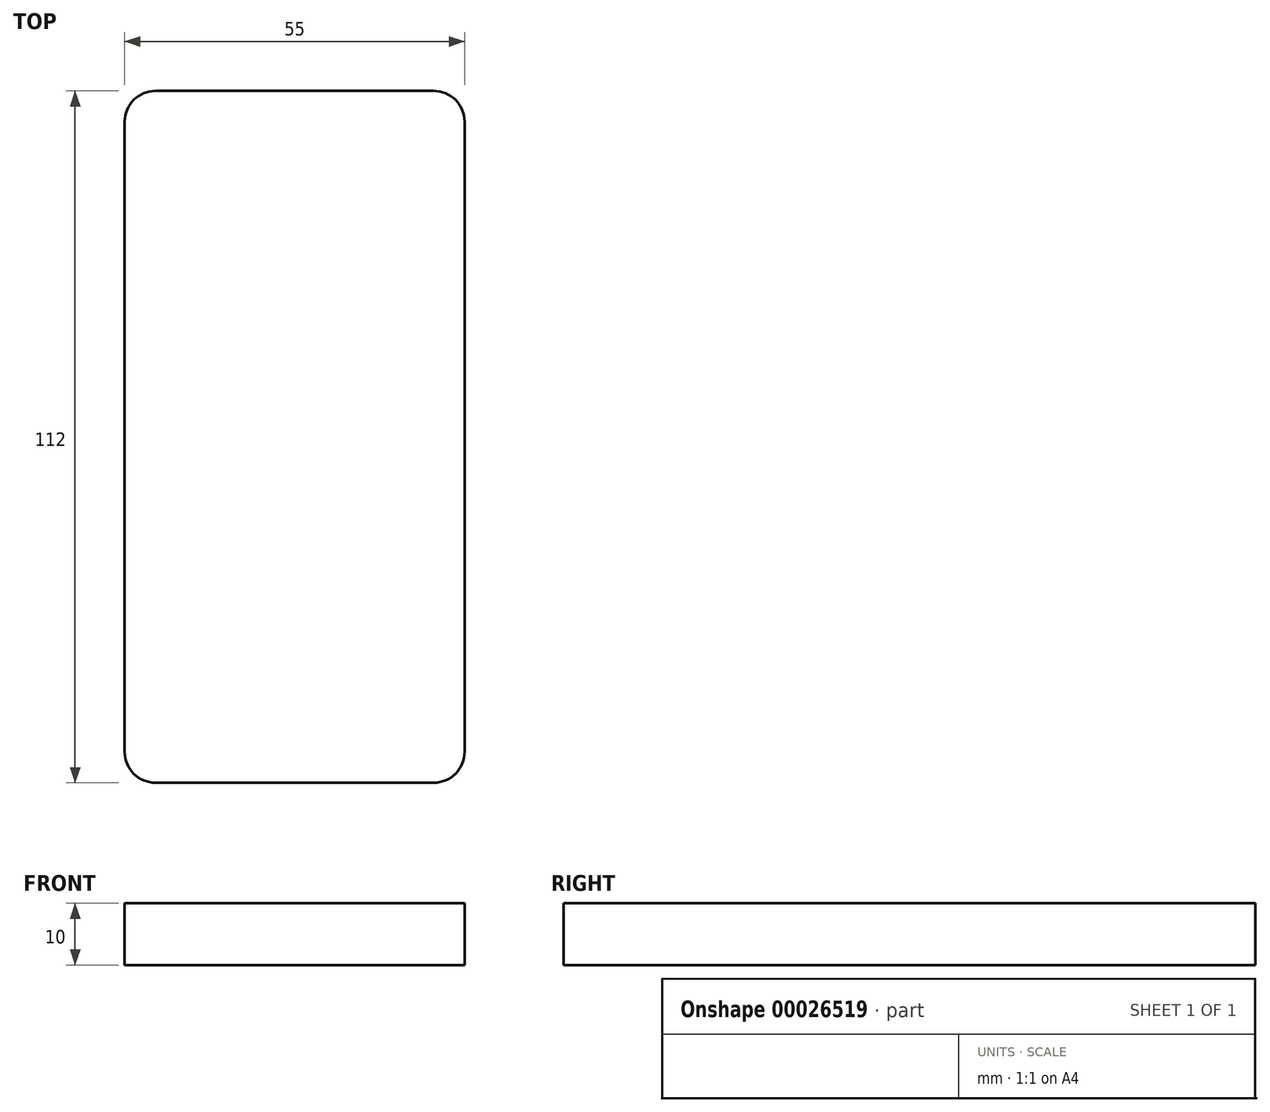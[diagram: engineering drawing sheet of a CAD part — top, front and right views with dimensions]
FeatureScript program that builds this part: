
annotation { "Feature Type Name" : "Feature", "Feature Type Description" : "" }
export const myFeature = defineFeature(function(context is Context, id is Id, definition is map)
    precondition{}
    {
        {
            var Q0;
            Q0=qCreatedBy(makeId("Top.planeOp"),FACE);
            var sketch = newSketch(context, id + "F0", { "sketchPlane" : qUnion([Q0])});
            skLineSegment(sketch, "E0.rect.bottom", {"start": v(-27.5, 56) * mm, "end": v(27.5, 56) * mm});
            skLineSegment(sketch, "E0.rect.top", {"start": v(-27.5, -56) * mm, "end": v(27.5, -56) * mm});
            skLineSegment(sketch, "E0.rect.left", {"start": v(-27.5, 56) * mm, "end": v(-27.5, -56) * mm});
            skLineSegment(sketch, "E0.rect.right", {"start": v(27.5, 56) * mm, "end": v(27.5, -56) * mm});
            skPoint(sketch, "E0.rect.middle", {"position": v(0, 0) * mm});
            skSolve(sketch);
        }
        {
            var Q0;
            Q0=makeQuery(id+"F0.imprint","IMPRINT",FACE,{"disambiguationData":[TD([[makeQuery(id+"F0.imprint","IMPRINT",EDGE,{"derivedFrom":sQuery(id+"F0.wireOp",EDGE,"E0.rect.bottom")}),-1.0]])]});
            extrude(context, id + "F1", {"entities" : qUnion([Q0]), "depth" : 10 * mm});
        }
        {
            var Q0;
            Q0=makeQuery(id+"F1.opExtrude","SWEPT_EDGE",EDGE,{"disambiguationData":[OSD([sQuery(id+"F0.wireOp",EDGE,"E0.rect.top"),sQuery(id+"F0.wireOp",EDGE,"E0.rect.left")])]});
            fillet(context, id + "F2", {"entities" : qUnion([Q0]), "radius" : 5 * mm, "tangentPropagation" : true, "allowEdgeOverflow" : false});
        }
        {
            var Q0;
            Q0=makeQuery(id+"F1.opExtrude","SWEPT_EDGE",EDGE,{"disambiguationData":[OSD([sQuery(id+"F0.wireOp",EDGE,"E0.rect.bottom"),sQuery(id+"F0.wireOp",EDGE,"E0.rect.left")])]});
            var Q1;
            Q1=makeQuery(id+"F1.opExtrude","SWEPT_EDGE",EDGE,{"disambiguationData":[OSD([sQuery(id+"F0.wireOp",EDGE,"E0.rect.top"),sQuery(id+"F0.wireOp",EDGE,"E0.rect.right")])]});
            fillet(context, id + "F3", {"entities" : qUnion([Q0, Q1]), "radius" : 5 * mm, "tangentPropagation" : true, "allowEdgeOverflow" : false});
        }
        {
            var Q0;
            Q0=makeQuery(id+"F1.opExtrude","SWEPT_EDGE",EDGE,{"disambiguationData":[OSD([sQuery(id+"F0.wireOp",EDGE,"E0.rect.bottom"),sQuery(id+"F0.wireOp",EDGE,"E0.rect.right")])]});
            fillet(context, id + "F4", {"entities" : qUnion([Q0]), "radius" : 5 * mm, "tangentPropagation" : true, "allowEdgeOverflow" : false});
        }
    });
